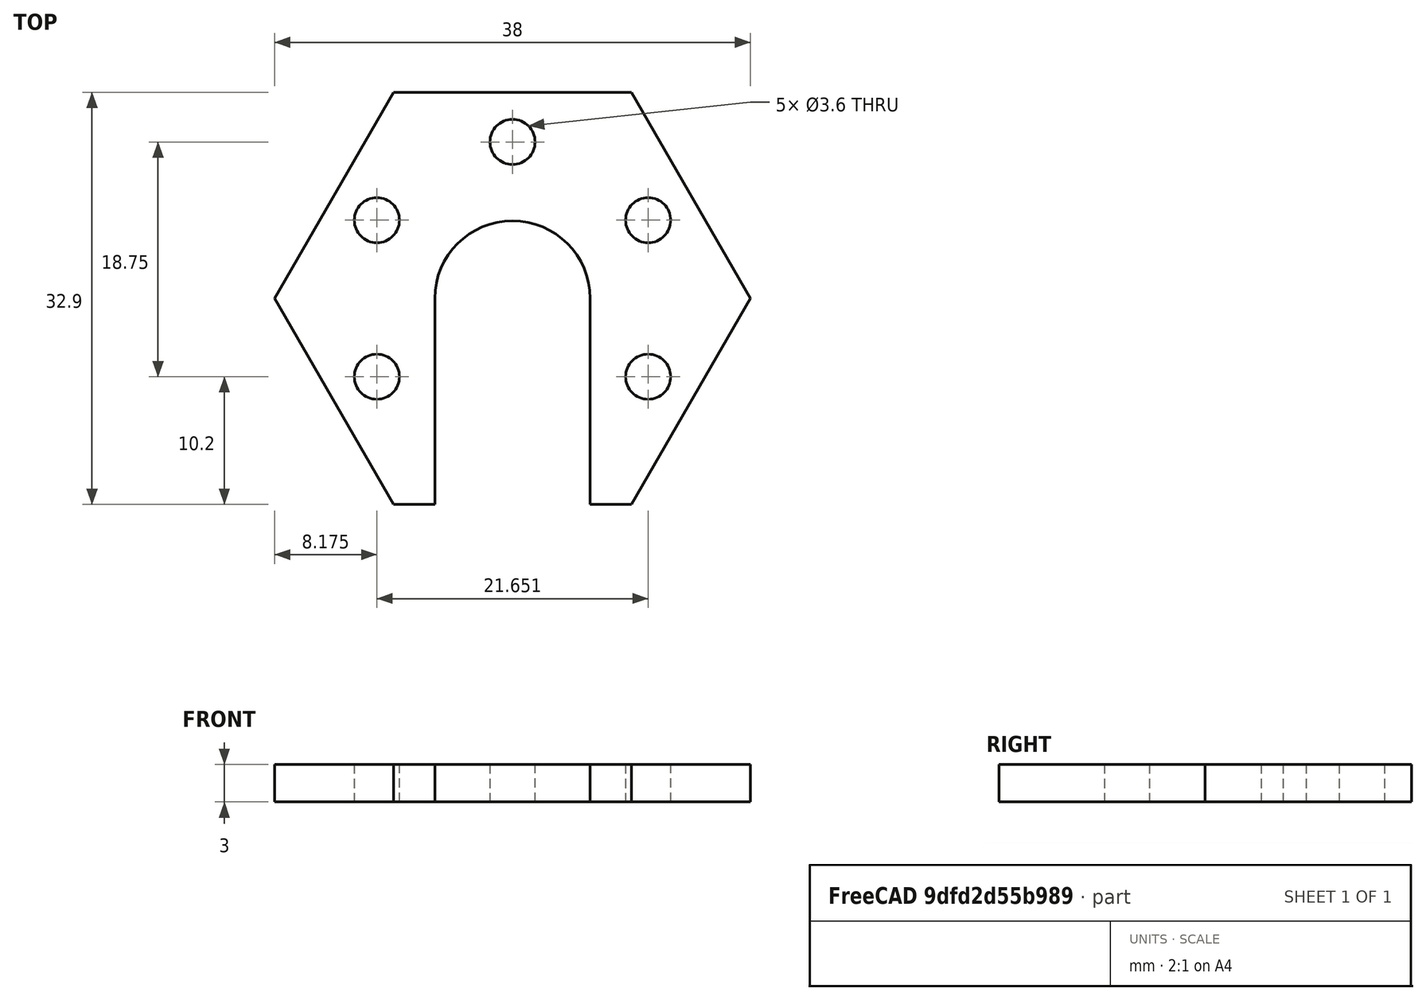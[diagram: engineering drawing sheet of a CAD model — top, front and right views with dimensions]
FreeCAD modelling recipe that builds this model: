
FCSTD DOCUMENT
Label: jheadGroovePlate
objects: Sketcher::SketchObject×2, PartDesign::Pad×1, Mesh::Feature×1
note: 4 computed .brp shape members not serialized (recipe doc carries the construction recipe); baked Part::Feature solids carry a one-line shape summary decoded from their .brp

FEATURE [Sketcher::SketchObject] Sketch
  sketch-geometry (25):
    g0: Circle [constr] CenterX=0 CenterY=0 CenterZ=0 NormalX=0 NormalY=0 NormalZ=1 Radius=12.5
    g1: LineSegment [constr] StartX=-10.8253 StartY=-6.25 StartZ=0 EndX=-10.8253 EndY=6.25 EndZ=0
    g2: LineSegment [constr] StartX=-10.8253 StartY=6.25 StartZ=0 EndX=0 EndY=12.5 EndZ=0
    g3: LineSegment [constr] StartX=0 StartY=12.5 StartZ=0 EndX=10.8253 EndY=6.25 EndZ=0
    g4: LineSegment [constr] StartX=10.8253 StartY=6.25 StartZ=0 EndX=10.8253 EndY=-6.25 EndZ=0
    g5: LineSegment [constr] StartX=10.8253 StartY=-6.25 StartZ=0 EndX=0 EndY=-12.5 EndZ=0
    g6: LineSegment [constr] StartX=0 StartY=-12.5 StartZ=0 EndX=-10.8253 EndY=-6.25 EndZ=0
    g7: Circle CenterX=0 CenterY=12.5 CenterZ=0 NormalX=0 NormalY=0 NormalZ=1 Radius=1.8
    g8: Circle CenterX=10.8253 CenterY=6.25 CenterZ=0 NormalX=0 NormalY=0 NormalZ=1 Radius=1.8
    g9: Circle CenterX=10.8253 CenterY=-6.25 CenterZ=0 NormalX=0 NormalY=0 NormalZ=1 Radius=1.8
    g10: Circle CenterX=-10.8253 CenterY=6.25 CenterZ=0 NormalX=0 NormalY=0 NormalZ=1 Radius=1.8
    g11: Circle CenterX=-10.8253 CenterY=-6.25 CenterZ=0 NormalX=0 NormalY=0 NormalZ=1 Radius=1.8
    g12: ArcOfCircle CenterX=0 CenterY=0 CenterZ=0 NormalX=0 NormalY=0 NormalZ=1 Radius=6.2 StartAngle=0 EndAngle=3.14159
    g13: LineSegment StartX=6.2 StartY=0 StartZ=0 EndX=6.2 EndY=-16.4545 EndZ=0
    g14: LineSegment StartX=-6.2 StartY=0 StartZ=0 EndX=-6.2 EndY=-16.4545 EndZ=0
    g15: LineSegment [constr] StartX=-6.2 StartY=0 StartZ=0 EndX=6.2 EndY=0 EndZ=0
    g16: Circle [constr] CenterX=0 CenterY=0 CenterZ=0 NormalX=0 NormalY=0 NormalZ=1 Radius=19
    g17: LineSegment StartX=-9.5 StartY=16.4545 StartZ=0 EndX=9.5 EndY=16.4545 EndZ=0
    g18: LineSegment StartX=9.5 StartY=16.4545 StartZ=0 EndX=19 EndY=-4e-12 EndZ=0
    g19: LineSegment StartX=19 StartY=-4e-12 StartZ=0 EndX=9.5 EndY=-16.4545 EndZ=0
    g20: LineSegment StartX=-9.5 StartY=-16.4545 StartZ=0 EndX=-19 EndY=-9e-12 EndZ=0
    g21: LineSegment StartX=-19 StartY=-9e-12 StartZ=0 EndX=-9.5 EndY=16.4545 EndZ=0
    g22: LineSegment StartX=-9.5 StartY=-16.4545 StartZ=0 EndX=-6.2 EndY=-16.4545 EndZ=0
    g23: LineSegment StartX=6.2 StartY=-16.4545 StartZ=0 EndX=9.5 EndY=-16.4545 EndZ=0
    g24: LineSegment [constr] StartX=9.5 StartY=16.4545 StartZ=0 EndX=9.5 EndY=-16.4545 EndZ=0
  constraints (67):
    c: PointOnObject(g1,g0)
    c: PointOnObject(g1,g0)
    c: Vertical(g1)
    c: Coincident(g1,g2)
    c: PointOnObject(g2,g0)
    c: Coincident(g2,g3)
    c: PointOnObject(g3,g0)
    c: Coincident(g3,g4)
    c: PointOnObject(g4,g0)
    c: Vertical(g4)
    c: Coincident(g4,g5)
    c: PointOnObject(g5,g0)
    c: Coincident(g5,g6)
    c: Coincident(g6,g1)
    c: Equal(g2,g1)
    c: Equal(g1,g6)
    c: Equal(g6,g5)
    c: Equal(g5,g4)
    c: Radius(g0) = 12.5
    c: DistanceX(g0) = 0
    c: DistanceY(g0) = 0
    c: Coincident(g7,g2)
    c: Coincident(g8,g3)
    c: Coincident(g9,g4)
    c: Coincident(g10,g1)
    c: Coincident(g11,g1)
    c: Equal(g7,g10)
    c: Equal(g10,g11)
    c: Equal(g9,g8)
    c: Radius(g7) = 1.8
    c: Coincident(g12,g0)
    c: Coincident(g13,g12)
    c: Coincident(g14,g12)
    c: Vertical(g14)
    c: Vertical(g13)
    c: Coincident(g15,g12)
    c: Coincident(g15,g12)
    c: Horizontal(g15)
    c: Radius(g12) = 6.2
    c: Equal(g8,g7)
    c: PointOnObject(g0,g15)
    c: Coincident(g16,g0)
    c: Horizontal(g17)
    c: Coincident(g17,g18)
    c: Coincident(g18,g19)
    c: Coincident(g20,g21)
    c: Coincident(g21,g17)
    c: Equal(g20,g21)
    c: Equal(g21,g17)
    c: Equal(g17,g18)
    c: Equal(g18,g19)
    c: PointOnObject(g18,g16)
    c: PointOnObject(g17,g16)
    c: PointOnObject(g19,g16)
    c: PointOnObject(g20,g16)
    c: Radius(g16) = 19
    c: Coincident(g22,g20)
    c: Coincident(g22,g14)
    c: Horizontal(g22)
    c: Horizontal(g23)
    c: Coincident(g23,g19)
    c: PointOnObject(g20,g16)
    c: Equal(g22,g23)
    c: Coincident(g24,g17)
    c: Coincident(g24,g19)
    c: Coincident(g13,g23)
    c: Vertical(g24)
FEATURE [PartDesign::Pad] Pad
  Length = 3
  MirroredExtent = false
  Sketch = -> Sketch
FEATURE [Mesh::Feature] effector
  Placement = pos=(0,0,-8) rot=(0,0,1;0rad)
FEATURE [Sketcher::SketchObject] Sketch001
  Placement = pos=(0,0,3) rot=(0,0,1;0rad)
  Support = -> Pad [Face17]
  sketch-geometry (37):
    g0: LineSegment StartX=7.82736 StartY=-7.98205 StartZ=0 EndX=7.82736 EndY=-4.51795 EndZ=0
    g1: LineSegment StartX=7.82736 StartY=-4.51795 StartZ=0 EndX=10.8274 EndY=-2.7859 EndZ=0
    g2: LineSegment StartX=10.8274 StartY=-2.7859 StartZ=0 EndX=13.8274 EndY=-4.51795 EndZ=0
    g3: LineSegment StartX=13.8274 StartY=-4.51795 StartZ=0 EndX=13.8274 EndY=-7.98205 EndZ=0
    g4: LineSegment StartX=13.8274 StartY=-7.98205 StartZ=0 EndX=10.8274 EndY=-9.7141 EndZ=0
    g5: LineSegment StartX=10.8274 StartY=-9.7141 StartZ=0 EndX=7.82736 EndY=-7.98205 EndZ=0
    g6: LineSegment [constr] StartX=7.82736 StartY=-4.51795 StartZ=0 EndX=10.8274 EndY=-6.25 EndZ=0
    g7: LineSegment [constr] StartX=10.8274 StartY=-6.25 StartZ=0 EndX=7.82736 EndY=-7.98205 EndZ=0
    g8: LineSegment [constr] StartX=13.8274 StartY=-7.98205 StartZ=0 EndX=10.8274 EndY=-6.25 EndZ=0
    g9: LineSegment [constr] StartX=10.8274 StartY=-6.25 StartZ=0 EndX=13.8274 EndY=-4.51795 EndZ=0
    g10: LineSegment [constr] StartX=10.8274 StartY=-6.25 StartZ=0 EndX=10.8274 EndY=-9.7141 EndZ=0
    g11: LineSegment StartX=-13.8233 StartY=-7.98205 StartZ=0 EndX=-13.8233 EndY=-4.51795 EndZ=0
    g12: LineSegment StartX=-13.8233 StartY=-4.51795 StartZ=0 EndX=-10.8233 EndY=-2.7859 EndZ=0
    g13: LineSegment StartX=-10.8233 StartY=-2.7859 StartZ=0 EndX=-7.82327 EndY=-4.51795 EndZ=0
    g14: LineSegment StartX=-7.82327 StartY=-4.51795 StartZ=0 EndX=-7.82327 EndY=-7.98205 EndZ=0
    g15: LineSegment StartX=-7.82327 StartY=-7.98205 StartZ=0 EndX=-10.8233 EndY=-9.7141 EndZ=0
    g16: LineSegment StartX=-10.8233 StartY=-9.7141 StartZ=0 EndX=-13.8233 EndY=-7.98205 EndZ=0
    g17: LineSegment [constr] StartX=-13.8233 StartY=-4.51795 StartZ=0 EndX=-10.8233 EndY=-6.25 EndZ=0
    g18: LineSegment [constr] StartX=-10.8233 StartY=-6.25 StartZ=0 EndX=-13.8233 EndY=-7.98205 EndZ=0
    g19: LineSegment [constr] StartX=-7.82327 StartY=-7.98205 StartZ=0 EndX=-10.8233 EndY=-6.25 EndZ=0
    g20: LineSegment [constr] StartX=-10.8233 StartY=-6.25 StartZ=0 EndX=-7.82327 EndY=-4.51795 EndZ=0
    g21: LineSegment [constr] StartX=-10.8233 StartY=-6.25 StartZ=0 EndX=-10.8233 EndY=-9.7141 EndZ=0
    g22: LineSegment StartX=-2.99795 StartY=10.7679 StartZ=0 EndX=-2.99795 EndY=14.2321 EndZ=0
    g23: LineSegment StartX=-2.99795 StartY=14.2321 StartZ=0 EndX=0.002046 EndY=15.9641 EndZ=0
    g24: LineSegment StartX=0.002046 StartY=15.9641 StartZ=0 EndX=3.00205 EndY=14.2321 EndZ=0
    g25: LineSegment StartX=3.00205 StartY=14.2321 StartZ=0 EndX=3.00205 EndY=10.7679 EndZ=0
    g26: LineSegment StartX=3.00205 StartY=10.7679 StartZ=0 EndX=0.002046 EndY=9.0359 EndZ=0
    g27: LineSegment StartX=0.002046 StartY=9.0359 StartZ=0 EndX=-2.99795 EndY=10.7679 EndZ=0
    g28: LineSegment [constr] StartX=-2.99795 StartY=14.2321 StartZ=0 EndX=0.002046 EndY=12.5 EndZ=0
    g29: LineSegment [constr] StartX=0.002046 StartY=12.5 StartZ=0 EndX=-2.99795 EndY=10.7679 EndZ=0
    g30: LineSegment [constr] StartX=3.00205 StartY=10.7679 StartZ=0 EndX=0.002046 EndY=12.5 EndZ=0
    g31: LineSegment [constr] StartX=0.002046 StartY=12.5 StartZ=0 EndX=3.00205 EndY=14.2321 EndZ=0
    g32: LineSegment [constr] StartX=0.002046 StartY=12.5 StartZ=0 EndX=0.002046 EndY=9.0359 EndZ=0
    g33: LineSegment [constr] StartX=0.002046 StartY=12.5 StartZ=0 EndX=-10.8233 EndY=-6.25 EndZ=0
    g34: LineSegment [constr] StartX=-10.8233 StartY=-6.25 StartZ=0 EndX=10.8274 EndY=-6.25 EndZ=0
    g35: LineSegment [constr] StartX=10.8274 StartY=-6.25 StartZ=0 EndX=0.002046 EndY=12.5 EndZ=0
    g36: Circle [constr] CenterX=0.002046 CenterY=0 CenterZ=0 NormalX=0 NormalY=0 NormalZ=1 Radius=12.5
  constraints (96):
    c: Vertical(g0)
    c: Coincident(g0,g1)
    c: Coincident(g1,g2)
    c: Coincident(g2,g3)
    c: Vertical(g3)
    c: Coincident(g3,g4)
    c: Coincident(g4,g5)
    c: Coincident(g5,g0)
    c: Coincident(g6,g0)
    c: Coincident(g6,g7)
    c: Coincident(g7,g0)
    c: Coincident(g8,g6)
    c: Coincident(g8,g9)
    c: Coincident(g9,g2)
    c: Coincident(g8,g3)
    c: Coincident(g10,g6)
    c: Coincident(g10,g4)
    c: Vertical(g10)
    c: Equal(g6,g7)
    c: Equal(g7,g10)
    c: Equal(g10,g8)
    c: Equal(g8,g9)
    c: Equal(g4,g5)
    c: Equal(g5,g0)
    c: Equal(g0,g1)
    c: Equal(g1,g2)
    c: DistanceX(g0,g3) = 6
    c: Vertical(g11)
    c: Coincident(g11,g12)
    c: Coincident(g12,g13)
    c: Coincident(g13,g14)
    c: Vertical(g14)
    c: Coincident(g14,g15)
    c: Coincident(g15,g16)
    c: Coincident(g16,g11)
    c: Coincident(g17,g11)
    c: Coincident(g17,g18)
    c: Coincident(g18,g11)
    c: Coincident(g19,g17)
    c: Coincident(g19,g20)
    c: Coincident(g20,g13)
    c: Coincident(g14,g19)
    c: Coincident(g21,g17)
    c: Coincident(g21,g15)
    c: Vertical(g21)
    c: Equal(g17,g18)
    c: Equal(g18,g21)
    c: Equal(g21,g19)
    c: Equal(g19,g20)
    c: Equal(g13,g12)
    c: Equal(g12,g11)
    c: Equal(g11,g16)
    c: Equal(g16,g15)
    c: DistanceX(g11,g14) = 6
    c: Vertical(g22)
    c: Coincident(g22,g23)
    c: Coincident(g23,g24)
    c: Coincident(g24,g25)
    c: Vertical(g25)
    c: Coincident(g25,g26)
    c: Coincident(g26,g27)
    c: Coincident(g27,g22)
    c: Coincident(g28,g22)
    c: Coincident(g28,g29)
    c: Coincident(g29,g22)
    c: Coincident(g30,g28)
    c: Coincident(g30,g31)
    c: Coincident(g31,g24)
    c: Coincident(g25,g30)
    c: Coincident(g32,g28)
    c: Coincident(g32,g26)
    c: Vertical(g32)
    c: Equal(g31,g30)
    c: Equal(g30,g32)
    c: Equal(g32,g29)
    c: Equal(g29,g28)
    c: Equal(g24,g23)
    c: Equal(g23,g22)
    c: Equal(g22,g26)
    c: Equal(g26,g27)
    c: DistanceX(g22,g25) = 6
    c: Coincident(g33,g28)
    c: Coincident(g33,g17)
    c: Coincident(g33,g34)
    c: Coincident(g34,g6)
    c: Horizontal(g34)
    c: Coincident(g34,g35)
    c: Coincident(g35,g28)
    c: Equal(g35,g33)
    c: Equal(g33,g34)
    c: PointOnObject(g28,g36)
    c: PointOnObject(g17,g36)
    c: PointOnObject(g6,g36)
    c: DistanceX(g36) = 0.002046
    c: DistanceY(g36) = 0
    c: Radius(g36) = 12.5
